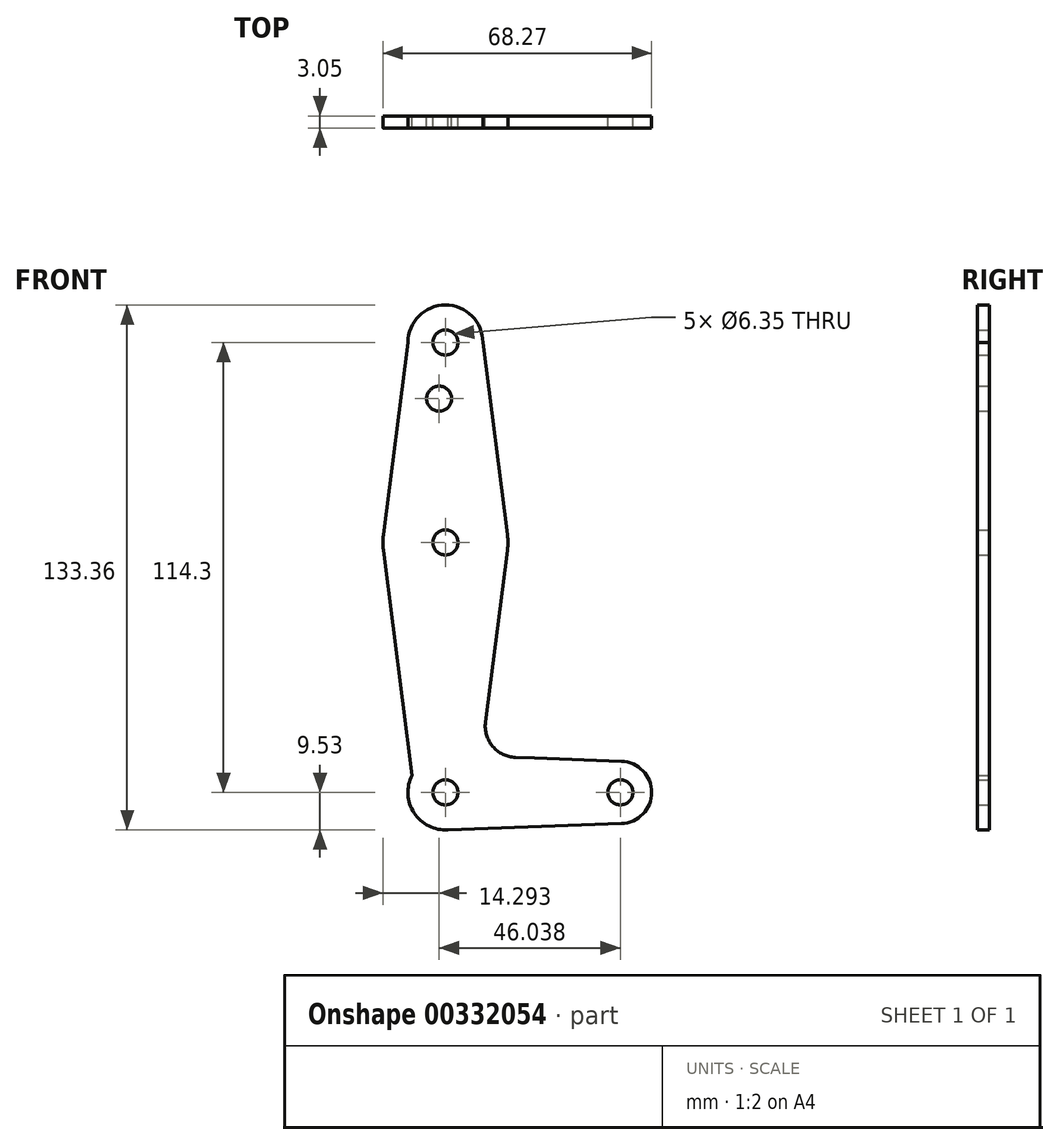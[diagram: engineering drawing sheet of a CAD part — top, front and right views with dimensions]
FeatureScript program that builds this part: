
annotation { "Feature Type Name" : "Feature", "Feature Type Description" : "" }
export const myFeature = defineFeature(function(context is Context, id is Id, definition is map)
    precondition{}
    {
        {
            var Q0;
            Q0=qCreatedBy(makeId("Front.planeOp"),FACE);
            var sketch = newSketch(context, id + "F0", { "sketchPlane" : qUnion([Q0])});
            skLineSegment(sketch, "E0", {"start": v(0, 0) * mm, "end": v(0, 114.3) * mm, "construction": true});
            skLineSegment(sketch, "E1", {"start": v(0, 0) * mm, "end": v(44.45, 0) * mm, "construction": true});
            skCircle(sketch, "E2", {"center": v(0, 114.3) * mm, "radius": 9.53 * mm});
            skCircle(sketch, "E3", {"center": v(0, 63.5) * mm, "radius": 15.88 * mm});
            skCircle(sketch, "E4", {"center": v(0, 0) * mm, "radius": 9.53 * mm});
            skCircle(sketch, "E5", {"center": v(44.45, 0) * mm, "radius": 7.94 * mm});
            skLineSegment(sketch, "E6", {"start": v(-9.53, 114.3) * mm, "end": v(-15.75, 65.5) * mm});
            skLineSegment(sketch, "E7", {"start": v(9.52, 114.3) * mm, "end": v(15.75, 65.5) * mm});
            skLineSegment(sketch, "E8", {"start": v(17.78, 8.9) * mm, "end": v(44.73, 7.93) * mm});
            skLineSegment(sketch, "E9", {"start": v(0, -9.53) * mm, "end": v(44.73, -7.93) * mm});
            skCircle(sketch, "E10", {"center": v(0, 114.3) * mm, "radius": 3.18 * mm});
            skCircle(sketch, "E11", {"center": v(0, 0) * mm, "radius": 3.18 * mm});
            skCircle(sketch, "E12", {"center": v(44.45, 0) * mm, "radius": 3.18 * mm});
            skCircle(sketch, "E13", {"center": v(-1.59, 100.03) * mm, "radius": 3.18 * mm});
            skCircle(sketch, "E14", {"center": v(0, 63.5) * mm, "radius": 3.18 * mm});
            skLineSegment(sketch, "E15", {"start": v(9.57, 0) * mm, "end": v(-9.57, 0) * mm, "construction": true});
            skLineSegment(sketch, "E16", {"start": v(15.75, 61.5) * mm, "end": v(10.18, 17.84) * mm});
            skLineSegment(sketch, "E17", {"start": v(-8.46, 4.37) * mm, "end": v(-15.75, 61.5) * mm});
            skPoint(sketch, "E18.newPointA", {"position": v(8.46, 4.37) * mm});
            skLineSegment(sketch, "E19", {"start": v(10.18, 17.84) * mm, "end": v(10.18, 17.84) * mm});
            skLineSegment(sketch, "E20", {"start": v(22.6, 8.72) * mm, "end": v(17.78, 8.9) * mm});
            skArc(sketch, "E21.filletArc", {"start": v(10.18, 17.84) * mm, "mid": v(12, 11.7) * mm, "end": v(17.78, 8.9) * mm});
            skSolve(sketch);
        }
        {
            var Q0;
            Q0 = qSketchRegion(id + "F0", true);
            extrude(context, id + "F1", {"entities" : qUnion([Q0]), "depth" : 3.05 * mm});
        }
    });
